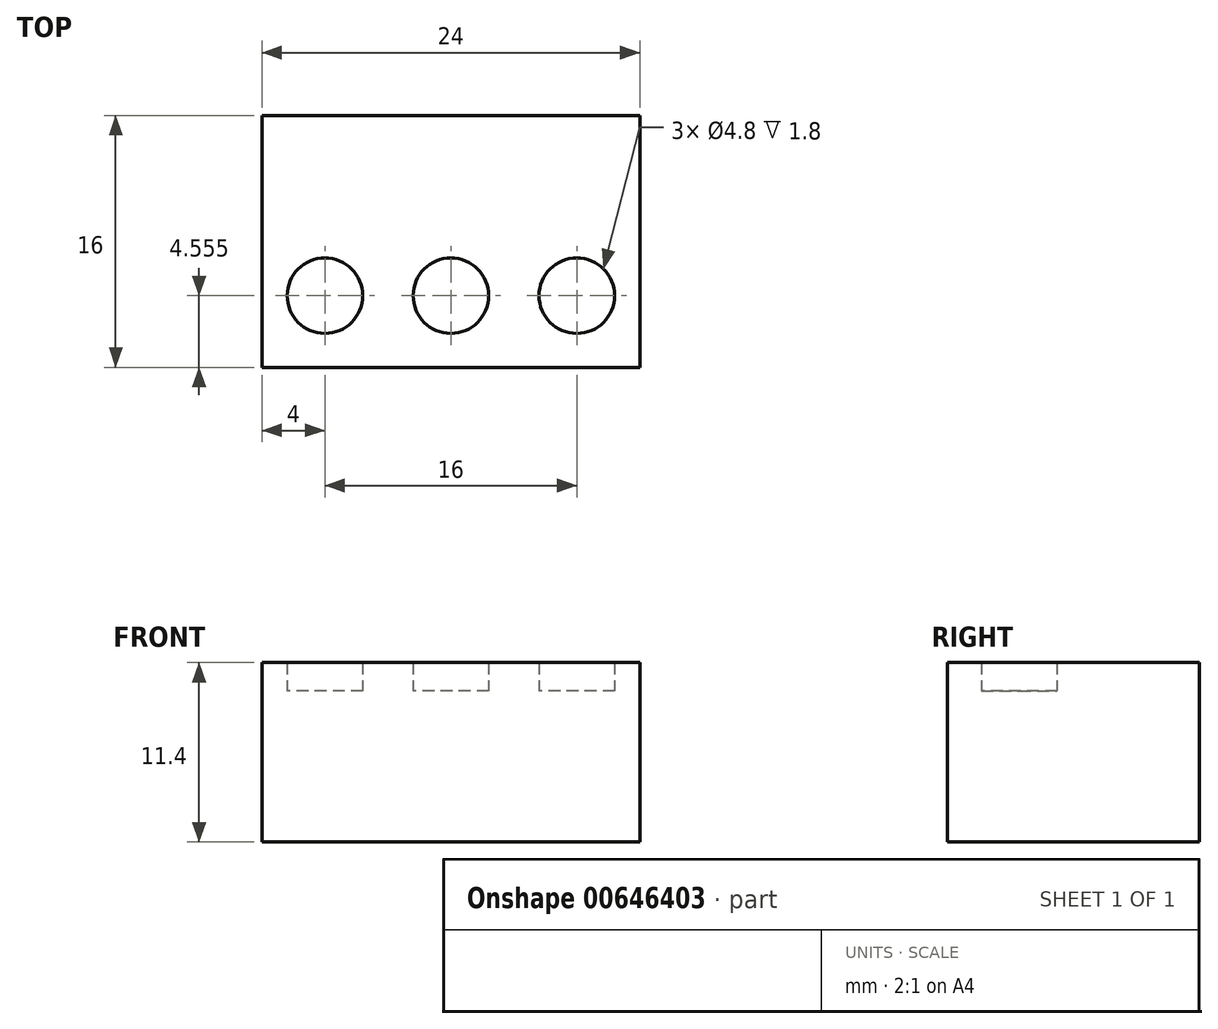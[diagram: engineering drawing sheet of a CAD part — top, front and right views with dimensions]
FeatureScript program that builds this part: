
annotation { "Feature Type Name" : "Feature", "Feature Type Description" : "" }
export const myFeature = defineFeature(function(context is Context, id is Id, definition is map)
    precondition{}
    {
        {
            var Q0;
            Q0=qCreatedBy(makeId("Top.planeOp"),FACE);
            var sketch = newSketch(context, id + "F0", { "sketchPlane" : qUnion([Q0])});
            skLineSegment(sketch, "E0.bottom", {"start": v(0, 0) * mm, "end": v(-24, 0) * mm});
            skLineSegment(sketch, "E0.top", {"start": v(0, 16) * mm, "end": v(-24, 16) * mm});
            skLineSegment(sketch, "E0.left", {"start": v(0, 0) * mm, "end": v(0, 16) * mm});
            skLineSegment(sketch, "E0.right", {"start": v(-24, 0) * mm, "end": v(-24, 16) * mm});
            skSolve(sketch);
        }
        {
            var Q0;
            Q0=makeQuery(id+"F0.imprint","IMPRINT",FACE,{"disambiguationData":[TD([[makeQuery(id+"F0.imprint","IMPRINT",EDGE,{"derivedFrom":sQuery(id+"F0.wireOp",EDGE,"E0.bottom")}),-1.0]])]});
            extrude(context, id + "F1", {"entities" : qUnion([Q0]), "depth" : 9.6 * mm, "offsetDistance" : 25.4 * mm});
        }
        {
            var Q0;
            Q0=makeQuery(id+"F1.opExtrude","CAP_FACE",FACE,{"disambiguationData":[OSD([sQuery(id+"F0.wireOp",EDGE,"E0.bottom"),sQuery(id+"F0.wireOp",EDGE,"E0.top"),sQuery(id+"F0.wireOp",EDGE,"E0.left"),sQuery(id+"F0.wireOp",EDGE,"E0.right")])],"isStart":false});
            var sketch = newSketch(context, id + "F2", { "sketchPlane" : qUnion([Q0])});
            skLineSegment(sketch, "E1", {"start": v(-24, 8.37) * mm, "end": v(0, 8.37) * mm, "construction": true});
            skLineSegment(sketch, "E2", {"start": v(-16, 16) * mm, "end": v(-16, 0) * mm, "construction": true});
            skLineSegment(sketch, "E3", {"start": v(-8, 16) * mm, "end": v(-8, 0) * mm, "construction": true});
            skLineSegment(sketch, "E4", {"start": v(-24, 16) * mm, "end": v(-16, 8.37) * mm, "construction": true});
            skLineSegment(sketch, "E5", {"start": v(-16, 8.37) * mm, "end": v(-8, 16) * mm, "construction": true});
            skLineSegment(sketch, "E6", {"start": v(-8, 16) * mm, "end": v(0, 8.37) * mm, "construction": true});
            skCircle(sketch, "E7", {"center": v(-20, 12.19) * mm, "radius": 2.4 * mm});
            skCircle(sketch, "E8", {"center": v(-12, 12.19) * mm, "radius": 2.4 * mm});
            skCircle(sketch, "E9", {"center": v(-4, 12.19) * mm, "radius": 2.4 * mm});
            skCircle(sketch, "E10.MirrorC", {"center": v(-20, 4.56) * mm, "radius": 2.4 * mm});
            skCircle(sketch, "E11.MirrorC", {"center": v(-12, 4.56) * mm, "radius": 2.4 * mm});
            skCircle(sketch, "E12.MirrorC", {"center": v(-4, 4.56) * mm, "radius": 2.4 * mm});
            skSolve(sketch);
        }
        {
            var Q0;
            Q0=makeQuery(id+"F2.imprint","IMPRINT",FACE,{"disambiguationData":[TD([[makeQuery(id+"F2.imprint","IMPRINT",EDGE,{"derivedFrom":sQuery(id+"F2.wireOp",EDGE,"E7")}),1.0]])]});
            var Q1;
            Q1=makeQuery(id+"F2.imprint","IMPRINT",FACE,{"disambiguationData":[TD([[makeQuery(id+"F2.imprint","IMPRINT",EDGE,{"derivedFrom":sQuery(id+"F2.wireOp",EDGE,"E8")}),1.0]])]});
            var Q2;
            Q2=makeQuery(id+"F2.imprint","IMPRINT",FACE,{"disambiguationData":[TD([[makeQuery(id+"F2.imprint","IMPRINT",EDGE,{"derivedFrom":sQuery(id+"F2.wireOp",EDGE,"E9")}),1.0]])]});
            var Q3;
            Q3=makeQuery(id+"F2.imprint","IMPRINT",FACE,{"disambiguationData":[TD([[makeQuery(id+"F2.imprint","IMPRINT",EDGE,{"derivedFrom":sQuery(id+"F2.wireOp",EDGE,"E12.MirrorC")}),-1.0]])]});
            var Q4;
            Q4=makeQuery(id+"F2.imprint","IMPRINT",FACE,{"disambiguationData":[TD([[makeQuery(id+"F2.imprint","IMPRINT",EDGE,{"derivedFrom":sQuery(id+"F2.wireOp",EDGE,"E11.MirrorC")}),-1.0]])]});
            var Q5;
            Q5=makeQuery(id+"F2.imprint","IMPRINT",FACE,{"disambiguationData":[TD([[makeQuery(id+"F2.imprint","IMPRINT",EDGE,{"derivedFrom":sQuery(id+"F2.wireOp",EDGE,"E10.MirrorC")}),-1.0]])]});
            var Q6;
            Q6=sQuery(id+"F2.wireOp",EDGE,"E7");
            extrude(context, id + "F3", {"entities" : qUnion([Q0, Q1, Q2, Q3, Q4, Q5]), "operationType" : NewBodyOperationType.ADD, "surfaceEntities" : qUnion([Q6]), "depth" : 1.8 * mm, "offsetDistance" : 25.4 * mm});
        }
    });
